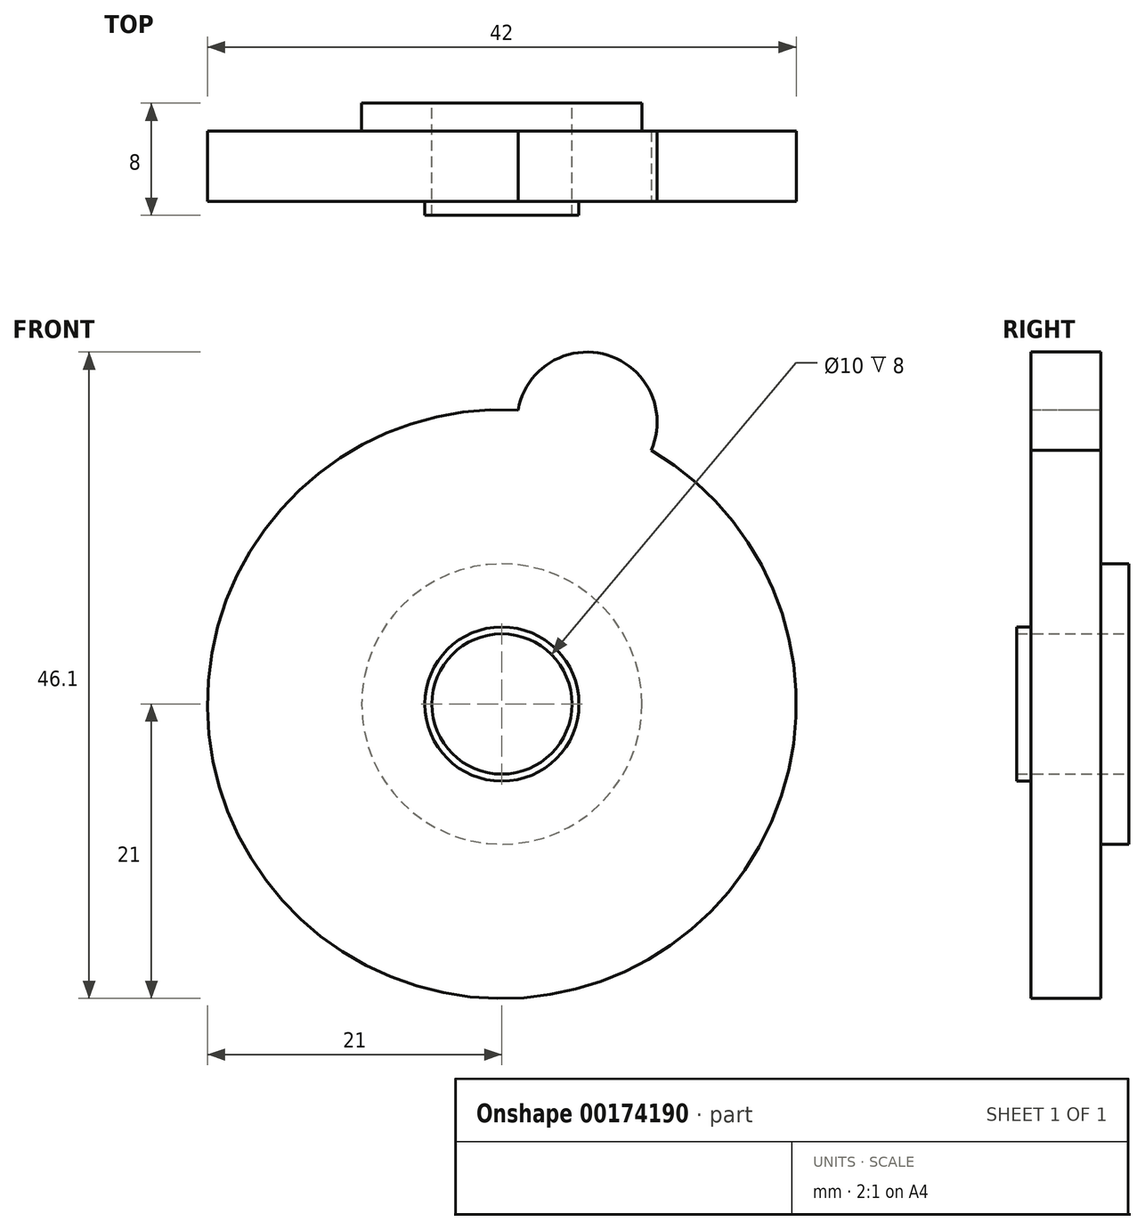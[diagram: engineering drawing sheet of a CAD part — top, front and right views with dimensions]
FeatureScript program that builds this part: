
annotation { "Feature Type Name" : "Feature", "Feature Type Description" : "" }
export const myFeature = defineFeature(function(context is Context, id is Id, definition is map)
    precondition{}
    {
        {
            var Q0;
            Q0=qCreatedBy(makeId("Front.planeOp"),FACE);
            var sketch = newSketch(context, id + "F0", { "sketchPlane" : qUnion([Q0])});
            skCircle(sketch, "E0", {"center": v(0, 0) * mm, "radius": 21 * mm});
            skCircle(sketch, "E1", {"center": v(0, 0) * mm, "radius": 20 * mm});
            skSolve(sketch);
        }
        {
            var Q0;
            Q0=sQuery(id+"F0.wireOp",EDGE,"E0");
            var Q1;
            Q1=sQuery(id+"F0.wireOp",EDGE,"E1");
            extrude(context, id + "F1", {"bodyType" : ToolBodyType.SURFACE, "surfaceEntities" : qUnion([Q0, Q1]), "depth" : 11 * mm});
        }
        {
            var Q0;
            Q0=qCreatedBy(makeId("Front.planeOp"),FACE);
            var sketch = newSketch(context, id + "F2", { "sketchPlane" : qUnion([Q0])});
            skCircle(sketch, "E2", {"center": v(0, 0) * mm, "radius": 21 * mm});
            skSolve(sketch);
        }
        {
            var Q0;
            Q0=makeQuery(id+"F2.imprint","IMPRINT",FACE,{"disambiguationData":[TD([[makeQuery(id+"F2.imprint","IMPRINT",EDGE,{"derivedFrom":sQuery(id+"F2.wireOp",EDGE,"E2")}),1.0]])]});
            extrude(context, id + "F3", {"entities" : qUnion([Q0]), "depth" : 3 * mm});
        }
        {
            var Q0;
            Q0=qCreatedBy(makeId("Front.planeOp"),FACE);
            var sketch = newSketch(context, id + "F4", { "sketchPlane" : qUnion([Q0])});
            skCircle(sketch, "E3", {"center": v(0, 0) * mm, "radius": 10 * mm});
            skSolve(sketch);
        }
        {
            var Q0;
            Q0=makeQuery(id+"F4.imprint","IMPRINT",FACE,{"disambiguationData":[TD([[makeQuery(id+"F4.imprint","IMPRINT",EDGE,{"derivedFrom":sQuery(id+"F4.wireOp",EDGE,"E3")}),1.0]])]});
            extrude(context, id + "F5", {"entities" : qUnion([Q0]), "operationType" : NewBodyOperationType.ADD, "oppositeDirection" : true, "depth" : 2 * mm});
        }
        {
            var Q0;
            Q0=makeQuery(id+"F5.opExtrude","CAP_FACE",FACE,{"disambiguationData":[OSD([sQuery(id+"F4.wireOp",EDGE,"E3")])],"isStart":false});
            var sketch = newSketch(context, id + "F6", { "sketchPlane" : qUnion([Q0])});
            skCircle(sketch, "E4", {"center": v(0, 0) * mm, "radius": 5 * mm});
            skSolve(sketch);
        }
        {
            var Q0;
            Q0 = qSketchRegion(id + "F6", true);
            extrude(context, id + "F7", {"entities" : qUnion([Q0]), "operationType" : NewBodyOperationType.REMOVE, "oppositeDirection" : true, "depth" : 25 * mm});
        }
        {
            var Q0;
            Q0=makeQuery(id+"F3.opExtrude","CAP_FACE",FACE,{"disambiguationData":[OSD([sQuery(id+"F2.wireOp",EDGE,"E2")])],"isStart":false});
            var sketch = newSketch(context, id + "F8", { "sketchPlane" : qUnion([Q0])});
            skCircle(sketch, "E5", {"center": v(6.08, 20.1) * mm, "radius": 5 * mm});
            skSolve(sketch);
        }
        {
            var Q0;
            Q0 = qSketchRegion(id + "F8", true);
            var Q1;
            {var subQ0=sQuery(id+"F8.wireOp",EDGE,"E5");var subQ1=makeQuery(id+"F3.opExtrude","CAP_EDGE",EDGE,{"disambiguationData":[OSD([sQuery(id+"F2.wireOp",EDGE,"E2")])],"isStart":false});var subQ2=makeQuery(id+"F8.imprint","INTERSECT",VERTEX,{"disambiguationData":[OD(0.0)],"derivedFrom":[subQ1,subQ0]});Q1=makeQuery(id+"F8.imprint","IMPRINT",FACE,{"disambiguationData":[TD([[makeQuery(id+"F8.imprint","IMPRINT",EDGE,{"disambiguationData":[TD([[subQ2,1.0]])],"derivedFrom":subQ0}),1.0]])]});}
            extrude(context, id + "F9", {"entities" : qUnion([Q0, Q1]), "operationType" : NewBodyOperationType.ADD, "oppositeDirection" : true, "depth" : 3 * mm});
        }
        {
            var Q0;
            Q0=makeQuery(id+"F9.boolean.opBoolean","MERGE",FACE,{"derivedFrom":[makeQuery(id+"F3.opExtrude","CAP_FACE",FACE,{"disambiguationData":[OSD([sQuery(id+"F2.wireOp",EDGE,"E2")])],"isStart":false}),makeQuery(id+"F9.opExtrude","CAP_FACE",FACE,{"disambiguationData":[OSD([sQuery(id+"F8.wireOp",EDGE,"E5")])],"isStart":true})]});
            var sketch = newSketch(context, id + "F10", { "sketchPlane" : qUnion([Q0])});
            skCircle(sketch, "E6", {"center": v(0, 0) * mm, "radius": 5.5 * mm});
            skSolve(sketch);
        }
        {
            var Q0;
            Q0=makeQuery(id+"F10.imprint","IMPRINT",FACE,{"disambiguationData":[TD([[makeQuery(id+"F10.imprint","IMPRINT",EDGE,{"derivedFrom":sQuery(id+"F10.wireOp",EDGE,"E6")}),-1.0]])]});
            var Q1;
            Q1=sQuery(id+"F10.wireOp",EDGE,"E6");
            extrude(context, id + "F11", {"entities" : qUnion([Q0]), "operationType" : NewBodyOperationType.ADD, "surfaceEntities" : qUnion([Q1]), "depth" : 1 * mm});
        }
        {
            var Q0;
            Q0=makeQuery(id+"F9.boolean.opBoolean","MERGE",FACE,{"derivedFrom":[makeQuery(id+"F3.opExtrude","CAP_FACE",FACE,{"disambiguationData":[OSD([sQuery(id+"F2.wireOp",EDGE,"E2")])],"isStart":false}),makeQuery(id+"F9.opExtrude","CAP_FACE",FACE,{"disambiguationData":[OSD([sQuery(id+"F8.wireOp",EDGE,"E5")])],"isStart":true})]});
            extrude(context, id + "F12", {"entities" : qUnion([Q0]), "operationType" : NewBodyOperationType.ADD, "depth" : 1 * mm});
        }
        {
            var Q0;
            {var subQ0=sQuery(id+"F8.wireOp",EDGE,"E5");var subQ1=sQuery(id+"F2.wireOp",EDGE,"E2");Q0=makeQuery(id+"F12.boolean.opBoolean","MERGE",FACE,{"derivedFrom":[makeQuery(id+"F11.opExtrude","CAP_FACE",FACE,{"disambiguationData":[OSD([subQ1,subQ0,sQuery(id+"F10.wireOp",EDGE,"E6")])],"isStart":false}),makeQuery(id+"F12.opExtrude","CAP_FACE",FACE,{"disambiguationData":[OSD([subQ1,subQ0])],"isStart":false})]});}
            var sketch = newSketch(context, id + "F13", { "sketchPlane" : qUnion([Q0])});
            skCircle(sketch, "E7", {"center": v(0, 0) * mm, "radius": 5.5 * mm});
            skSolve(sketch);
        }
        {
            var Q0;
            Q0=makeQuery(id+"F13.imprint","IMPRINT",FACE,{"disambiguationData":[TD([[makeQuery(id+"F13.imprint","IMPRINT",EDGE,{"derivedFrom":makeQuery(id+"F12.opExtrude","CAP_EDGE",EDGE,{"disambiguationData":[OSD([sQuery(id+"F2.wireOp",EDGE,"E2"),sQuery(id+"F6.wireOp",EDGE,"E4")])],"isStart":false})}),1.0]])]});
            var Q1;
            Q1=makeQuery(id+"F13.imprint","IMPRINT",FACE,{"disambiguationData":[TD([[makeQuery(id+"F13.imprint","IMPRINT",EDGE,{"derivedFrom":sQuery(id+"F13.wireOp",EDGE,"E7")}),-1.0]])]});
            extrude(context, id + "F14", {"entities" : qUnion([Q0, Q1]), "operationType" : NewBodyOperationType.ADD, "depth" : 1 * mm});
        }
        {
            var Q0;
            Q0=makeQuery(id+"F14.opExtrude","CAP_FACE",FACE,{"disambiguationData":[OSD([sQuery(id+"F2.wireOp",EDGE,"E2"),sQuery(id+"F6.wireOp",EDGE,"E4")])],"isStart":false});
            var sketch = newSketch(context, id + "F15", { "sketchPlane" : qUnion([Q0])});
            skCircle(sketch, "E8", {"center": v(0, 0) * mm, "radius": 5 * mm});
            skSolve(sketch);
        }
        {
            var Q0;
            Q0=makeQuery(id+"F15.imprint","IMPRINT",FACE,{"disambiguationData":[TD([[makeQuery(id+"F15.imprint","IMPRINT",EDGE,{"derivedFrom":sQuery(id+"F15.wireOp",EDGE,"E8")}),1.0]])]});
            extrude(context, id + "F16", {"entities" : qUnion([Q0]), "operationType" : NewBodyOperationType.REMOVE, "oppositeDirection" : true, "depth" : 1 * mm});
        }
        {
            var Q0;
            {var subQ0=sQuery(id+"F8.wireOp",EDGE,"E5");var subQ1=sQuery(id+"F2.wireOp",EDGE,"E2");Q0=makeQuery(id+"F12.boolean.opBoolean","MERGE",FACE,{"derivedFrom":[makeQuery(id+"F11.opExtrude","CAP_FACE",FACE,{"disambiguationData":[OSD([subQ1,subQ0,sQuery(id+"F10.wireOp",EDGE,"E6")])],"isStart":false}),makeQuery(id+"F12.opExtrude","CAP_FACE",FACE,{"disambiguationData":[OSD([subQ1,subQ0])],"isStart":false})]});}
            extrude(context, id + "F17", {"entities" : qUnion([Q0]), "operationType" : NewBodyOperationType.ADD, "depth" : 2 * mm});
        }
    });
